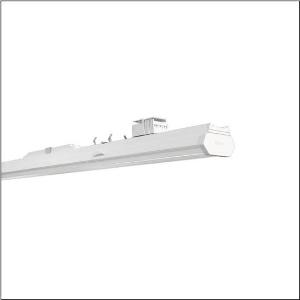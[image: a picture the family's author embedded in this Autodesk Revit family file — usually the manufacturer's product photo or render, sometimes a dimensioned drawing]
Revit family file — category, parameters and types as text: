
# Revit family: licross_r__11_protected_mo_51tp12mn4axg_95e7
name_source: partatom
category: Lighting Fixtures
units: mm (PartAtom-declared; Revit-internal decimal feet)

## family parameters
Cut with Voids When Loaded = No
Host = Face
Light Source = No
Part Type = Normal
Room Calculation Point = No
Round Connector Dimension = Use Diameter
Shared = No

## types (1)
- --- (1 x LED, 10020 lm, 55.3 W, 4000K)
    Apparent Load = 55 VA
    CIE Flux Codes = 73 92 98 99 100
    Color Rendering = 80
    Color Temperature = 4000K
    Default Elevation = 1800 mm
    Description = Licross® 11 Protected MO, luminaire insert, of sheet steel, galvanised, coil coated, white, length: 1.500mm, width: 90mm, height: 101mm, LED rated luminous flux: 10.030lm, light colour: 840, control gear: ON/OFF Multilumen, with plug, 3-pole, with phase selection, mains connection: 220..240V, AC, 50/60Hz, rated input power: 55W, halogen-free wiring, primary light control with lens, of plastic, primary optical cover: cover, of PMMA, light emission: direct distribution, primary light characteristic: symmetric, protection rating (complete): IP64, insulation class (complete): insulation class I (protective earthing), certification: CE, ENEC, VDE, UKCA, protection symbol: D if used in an environment with conductive dust loads with corresponding accessories, impact resistance: IK06, permissible ambient temperature for indoor applications: -35..+40°C, corresponds to IFS (International Featured Standards) requirements for safety and quality in the food industry, reducing of maximum allowable ambient temperature of 5°C with ceiling mounting, LABS conformity tested according to VDMA 24364:2018-05, packaging unit: 1 piece
    Height = 92 mm
    Lamp = 1 x LED
    Lamp Light Flux = 10020 lm
    Lamp Power = 55.3 W
    Lamp count = 1
    Length = 1500 mm
    Luminous efficacy = 181 lm/W
    Manufacturer = Siteco
    ModVariant = No
    Model = 51TP12MN4AXG
    Mounting Place = Ceiling
    Mounting Type = Pendant
    Number of Poles = 1
    OnlyDefault = Yes
    Power Factor = 1
    Product Name = Licross® 11 Protected MO
    Product group = luminaire insert
    ProductGroupID = 901
    Protection Class = Protection class I
    Protection Degree = IP 64
    RLX_Detail_Level = 1
    RLX_Emergency_Light_Flux = 0 lm
    RLX_Emergency_Type = 0
    RLX_Emergency_Type_DB = No
    RlxData = <blob elided: 22057 chars, md5=02cbf74c>
    Socket = socket
    Standby Power = 0 W
    System Light Flux = 10020 lm
    System Power = 55 W
    Type Comments = factory setting: luminous flux: 100 % | (A | C | E) | 126 mA
    Type Image = l_1256148.jpg
    URL = http://relux.com
    VarID = @adj_038107
    Voltage = 0 V
    Weight = 0.00 kg
    Width = 88 mm

## geometry (parser evidence)
native form markers: Blend x4, Sweep x12
no freeform markers — native parametric forms only
